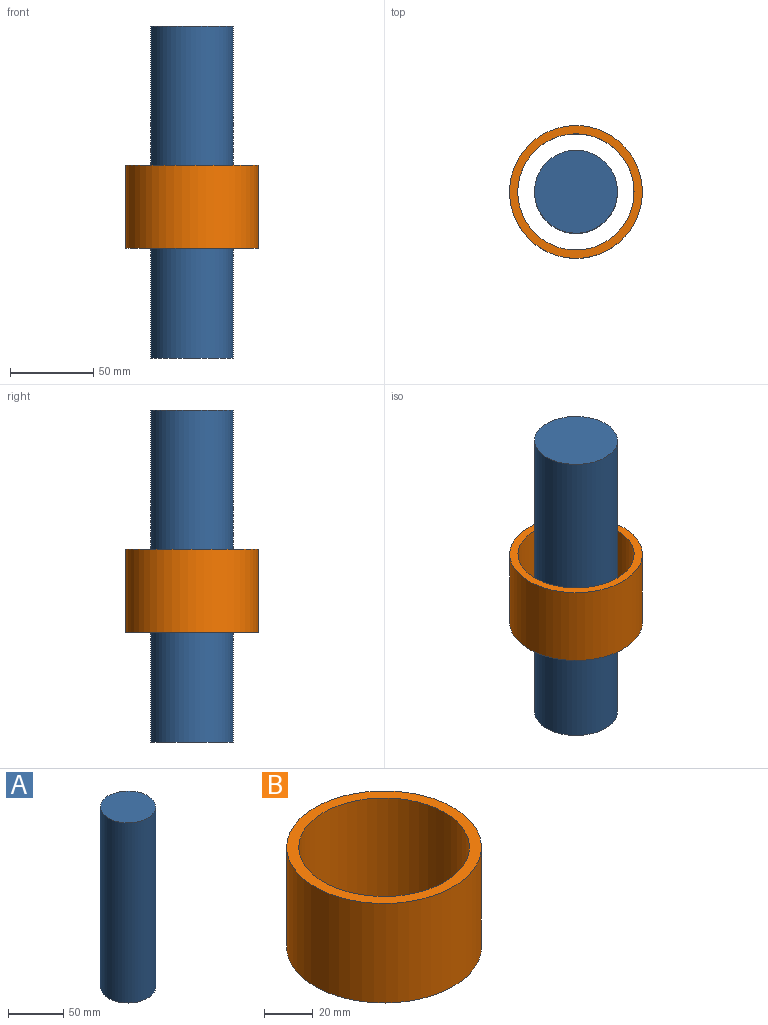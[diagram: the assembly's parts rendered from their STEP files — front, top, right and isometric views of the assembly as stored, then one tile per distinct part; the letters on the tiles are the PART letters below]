
ASSEMBLY  parts=2 mates=1
PART A: 3 faces, bbox 50x50x200 mm
  f0: cylinder r=25mm len=200mm, axis (0,0,-1), area 31415.9mm2, adj f1,f2
  f1: plane 50x50mm, normal (0,0,1), area 1963.5mm2, adj f0
  f2: plane 50x50mm, normal (0,0,-1), area 1963.5mm2, adj f0
PART B: 4 faces, bbox 80x80x50 mm
  f0: cylinder r=35mm len=70mm, axis (0,0,-1), area 10995.6mm2, adj f2,f3
  f1: cylinder r=40mm len=80mm, axis (0,0,-1), area 12566.4mm2, adj f2,f3
  f2: plane 80x80mm, normal (0,0,1), area 1178.1mm2, adj f0,f1
  f3: plane 80x80mm, normal (0,0,-1), area 1178.1mm2, adj f0,f1
PLACE A t=(6.16,63.17,20.69)mm fixed
PLACE B t=(6.16,63.17,86.67)mm
MATE slider A.f0 <-> B.f0  axis (0,0,-1) through (6.16,63.17,120.69)mm
